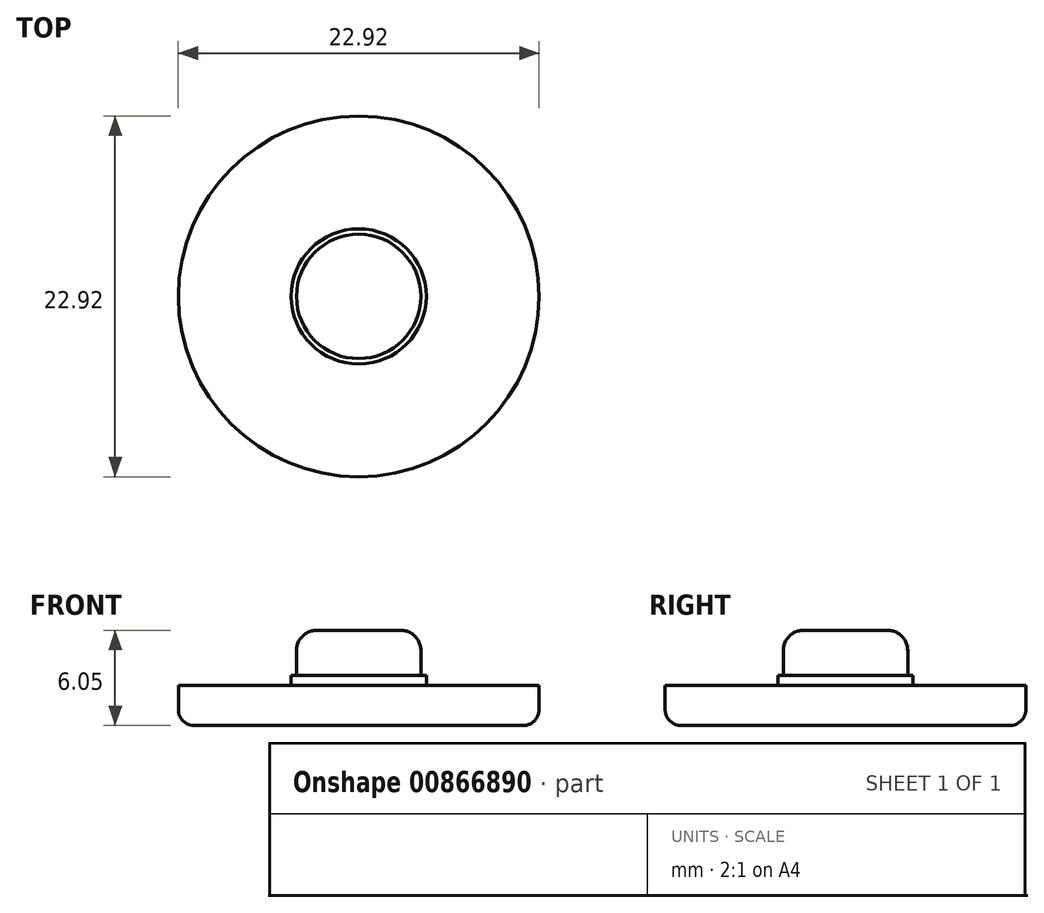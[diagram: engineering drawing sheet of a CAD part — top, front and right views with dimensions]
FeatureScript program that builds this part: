
annotation { "Feature Type Name" : "Feature", "Feature Type Description" : "" }
export const myFeature = defineFeature(function(context is Context, id is Id, definition is map)
    precondition{}
    {
        {
            var Q0;
            Q0=qCreatedBy(makeId("Top.planeOp"),FACE);
            var sketch = newSketch(context, id + "F0", { "sketchPlane" : qUnion([Q0])});
            skCircle(sketch, "E0", {"center": v(0, 0) * mm, "radius": 11.46 * mm});
            skCircle(sketch, "E1", {"center": v(0, 0) * mm, "radius": 3.95 * mm});
            skSolve(sketch);
        }
        {
            var Q0;
            Q0=makeQuery(id+"F0.imprint","IMPRINT",FACE,{"disambiguationData":[TD([[makeQuery(id+"F0.imprint","IMPRINT",EDGE,{"derivedFrom":sQuery(id+"F0.wireOp",EDGE,"E1")}),1.0]])]});
            extrude(context, id + "F1", {"entities" : qUnion([Q0]), "depth" : 6.05 * mm, "offsetDistance" : 25.4 * mm});
        }
        {
            var Q0;
            Q0=makeQuery(id+"F0.imprint","IMPRINT",FACE,{"disambiguationData":[TD([[makeQuery(id+"F0.imprint","IMPRINT",EDGE,{"derivedFrom":sQuery(id+"F0.wireOp",EDGE,"E0")}),1.0]])]});
            extrude(context, id + "F2", {"entities" : qUnion([Q0]), "operationType" : NewBodyOperationType.ADD, "depth" : 2.54 * mm, "offsetDistance" : 25.4 * mm});
        }
        {
            var Q0;
            Q0=makeQuery(id+"F2.opExtrude","CAP_EDGE",EDGE,{"disambiguationData":[OSD([sQuery(id+"F0.wireOp",EDGE,"E0")])],"isStart":true});
            fillet(context, id + "F3", {"entities" : qUnion([Q0]), "radius" : 1.02 * mm, "tangentPropagation" : true, "allowEdgeOverflow" : false});
        }
        {
            var Q0;
            Q0=makeQuery(id+"F1.opExtrude","CAP_EDGE",EDGE,{"disambiguationData":[OSD([sQuery(id+"F0.wireOp",EDGE,"E1")])],"isStart":false});
            fillet(context, id + "F4", {"entities" : qUnion([Q0]), "radius" : 1.27 * mm, "tangentPropagation" : true, "allowEdgeOverflow" : false});
        }
        {
            var Q0;
            Q0=makeQuery(id+"F2.opExtrude","CAP_FACE",FACE,{"disambiguationData":[OSD([sQuery(id+"F0.wireOp",EDGE,"E0"),sQuery(id+"F0.wireOp",EDGE,"E1")])],"isStart":false});
            var sketch = newSketch(context, id + "F5", { "sketchPlane" : qUnion([Q0])});
            skCircle(sketch, "E2", {"center": v(0, 0) * mm, "radius": 4.3 * mm});
            skSolve(sketch);
        }
        {
            var Q0;
            Q0=makeQuery(id+"F5.imprint","IMPRINT",FACE,{"disambiguationData":[TD([[makeQuery(id+"F5.imprint","IMPRINT",EDGE,{"derivedFrom":sQuery(id+"F5.wireOp",EDGE,"E2")}),1.0]])]});
            extrude(context, id + "F6", {"entities" : qUnion([Q0]), "operationType" : NewBodyOperationType.ADD, "depth" : 0.64 * mm, "offsetDistance" : 25.4 * mm});
        }
    });
